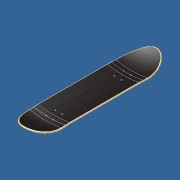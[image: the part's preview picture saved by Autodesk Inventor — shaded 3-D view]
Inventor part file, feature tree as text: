
AUTODESK INVENTOR PART (.ipt)
format: ipt  version: unknown  size: 539,136 bytes
history: native  units: mm
features: other x5, sketch x4, extrude x2, sweep x1, fillet x1
ambient origin geometry x8: Origin, YZ Plane, XZ Plane, XY Plane, X Axis, Y Axis, Z Axis, Center Point
feature tree (13):
  sketch  "Schizzo1"
  sketch  "Schizzo2"
  other  "Piano di lavoro1"
  sweep  "Sweep5"
  extrude  "Estrusione9"  Depth=410.0mm
  fillet  "Raccordo3"  Radius=50.0mm
  extrude  "Estrusione10"  Depth=2.5mm
  other  "Piano di lavoro4"
  sketch  "Schizzo15"
  other  "Linea chiusa proiettata27"
  other  "Linea chiusa proiettata28"
  sketch  "Schizzo16"
  other  "Linea chiusa proiettata29"
